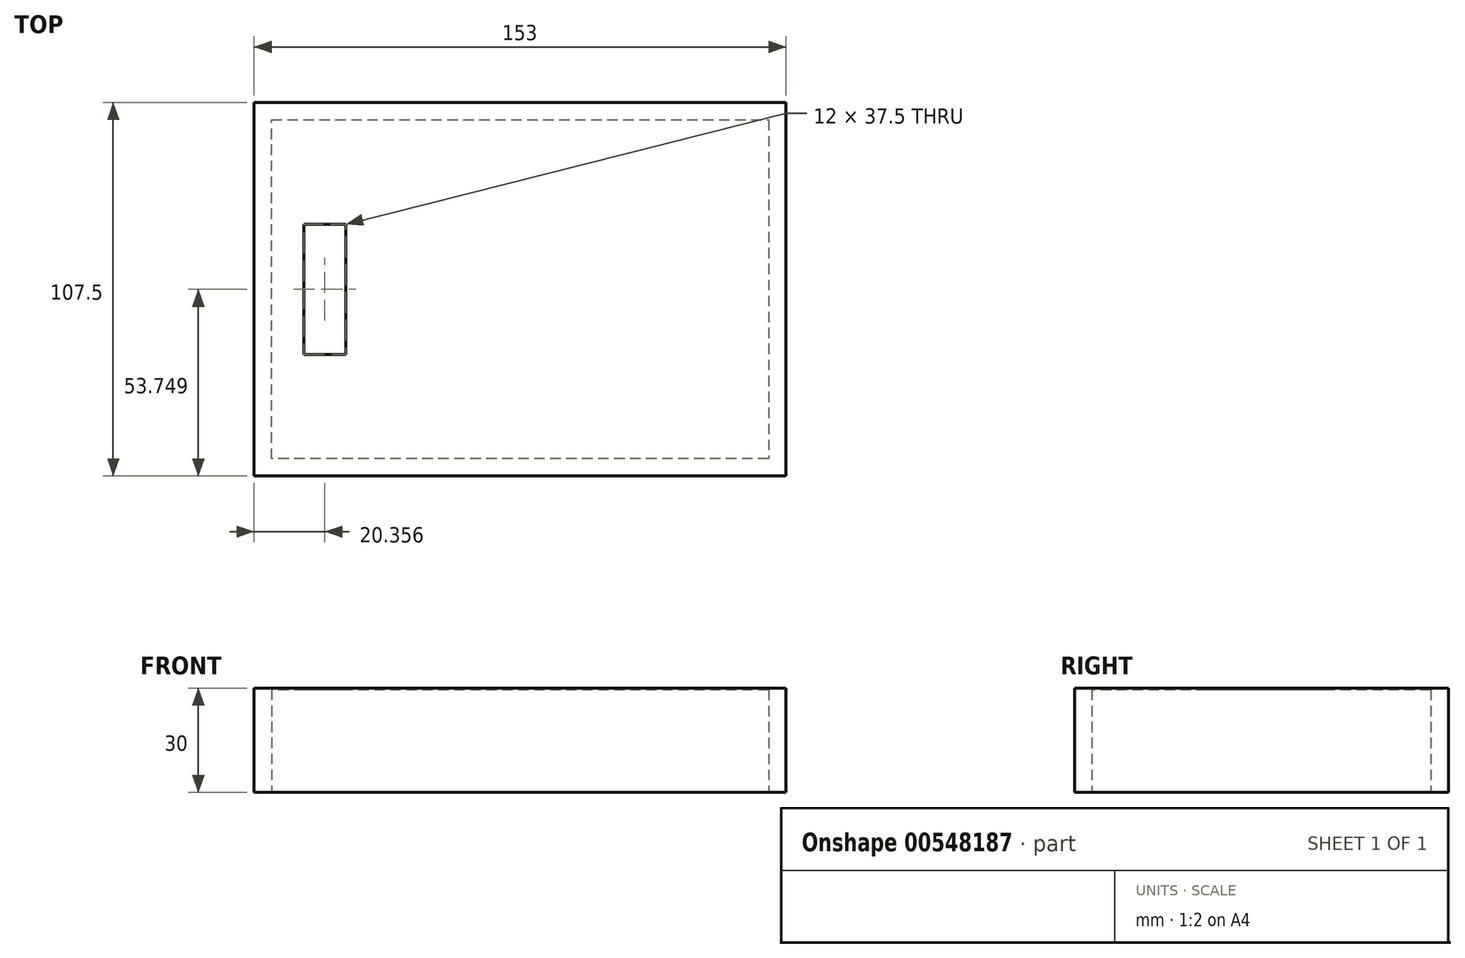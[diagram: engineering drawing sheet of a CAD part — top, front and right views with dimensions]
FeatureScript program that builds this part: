
annotation { "Feature Type Name" : "Feature", "Feature Type Description" : "" }
export const myFeature = defineFeature(function(context is Context, id is Id, definition is map)
    precondition{}
    {
        {
            var Q0;
            Q0=qCreatedBy(makeId("Top.planeOp"),FACE);
            var sketch = newSketch(context, id + "F0", { "sketchPlane" : qUnion([Q0])});
            skLineSegment(sketch, "E0.bottom", {"start": v(76.5, 53.75) * mm, "end": v(-76.5, 53.75) * mm});
            skLineSegment(sketch, "E0.top", {"start": v(76.5, -53.75) * mm, "end": v(-76.5, -53.75) * mm});
            skLineSegment(sketch, "E0.left", {"start": v(76.5, 53.75) * mm, "end": v(76.5, -53.75) * mm});
            skLineSegment(sketch, "E0.right", {"start": v(-76.5, 53.75) * mm, "end": v(-76.5, -53.75) * mm});
            skPoint(sketch, "E0.middle", {"position": v(0, 0) * mm});
            skLineSegment(sketch, "E1", {"start": v(-62.14, 18.75) * mm, "end": v(-62.14, -18.75) * mm});
            skLineSegment(sketch, "E2", {"start": v(-62.14, -18.75) * mm, "end": v(-50.14, -18.75) * mm});
            skLineSegment(sketch, "E3", {"start": v(-50.14, 18.75) * mm, "end": v(-62.14, 18.75) * mm});
            skLineSegment(sketch, "E4", {"start": v(-50.14, 18.75) * mm, "end": v(-50.14, 0) * mm});
            skLineSegment(sketch, "E5", {"start": v(-50.14, 0) * mm, "end": v(-50.14, 6.4) * mm});
            skLineSegment(sketch, "E6", {"start": v(-50.14, 6.4) * mm, "end": v(-50.14, -18.75) * mm});
            skSolve(sketch);
        }
        {
            var Q0;
            Q0=makeQuery(id+"F0.imprint","IMPRINT",FACE,{"disambiguationData":[TD([[makeQuery(id+"F0.imprint","IMPRINT",EDGE,{"derivedFrom":sQuery(id+"F0.wireOp",EDGE,"E0.bottom")}),1.0]])]});
            extrude(context, id + "F1", {"entities" : qUnion([Q0]), "depth" : 30 * mm, "offsetDistance" : 25.4 * mm});
        }
        {
            var Q0;
            Q0=qCreatedBy(makeId("Top.planeOp"),FACE);
            var sketch = newSketch(context, id + "F2", { "sketchPlane" : qUnion([Q0])});
            skLineSegment(sketch, "E7", {"start": v(71.5, -48.75) * mm, "end": v(-71.5, -48.75) * mm});
            skLineSegment(sketch, "E8", {"start": v(-71.5, -48.75) * mm, "end": v(-71.5, 48.75) * mm});
            skLineSegment(sketch, "E9", {"start": v(-71.5, 48.75) * mm, "end": v(71.5, 48.75) * mm});
            skLineSegment(sketch, "E10", {"start": v(71.5, 48.75) * mm, "end": v(71.5, -48.75) * mm});
            skSolve(sketch);
        }
        {
            var Q0;
            Q0=makeQuery(id+"F2.imprint","IMPRINT",FACE,{"disambiguationData":[TD([[makeQuery(id+"F2.imprint","IMPRINT",EDGE,{"derivedFrom":sQuery(id+"F2.wireOp",EDGE,"E7")}),-1.0]])]});
            extrude(context, id + "F3", {"entities" : qUnion([Q0]), "operationType" : NewBodyOperationType.REMOVE, "depth" : 29.5 * mm, "offsetDistance" : 25.4 * mm});
        }
    });
